# Revit family: Lodlinor
name_source: partatom
category: Generic Models
units: mm (PartAtom-declared; Revit-internal decimal feet)

## family parameters
Always vertical = Yes
Can host rebar = No
Cut with Voids When Loaded = No
Part Type = Normal
Room Calculation Point = No
Round Connector Dimension = Use Diameter
Shared = No
Work Plane-Based = No

## types (7) — shared parameters
2 = No
Height = 7000 mm  [stored 22.9659 ft]
Height_to_wheel = 6880 mm
Manufacturer = Saxi Vägg AB
URL = www.saxi.se
langd_rep = 6410 mm  [stored 21.0302 ft]

## per-type parameters (varying)
| type | 10 | 5 | 6 | 7 | 8 | 9 | Length_straight | NO_ROPES | beam_length |
| Saxi Lodlinor 4 | No | No | No | No | No | No | 2550 mm  [stored 8.36614 ft] | 4 | 4000 mm  [stored 13.1234 ft] |
| Saxi Lodlinor 5 | No | Yes | No | No | No | No | 3297 mm  [stored 10.8169 ft] | 5 | 4570 mm  [stored 14.9934 ft] |
| Saxi Lodlinor 6 | No | No | Yes | No | No | No | 3947 mm  [stored 12.9495 ft] | 6 | 5000 mm  [stored 16.4042 ft] |
| Saxi Lodlinor 7 | No | Yes | No | Yes | No | No | 4335 mm  [stored 14.2224 ft] | 7 | 5700 mm  [stored 18.7008 ft] |
| Saxi Lodlinor 8 | No | No | Yes | No | Yes | No | 5026 mm  [stored 16.4895 ft] | 8 | 6500 mm  [stored 21.3255 ft] |
| Saxi Lodlinor 9 | No | No | Yes | No | Yes | Yes | 5769 mm  [stored 18.9272 ft] | 9 | 7000 mm  [stored 22.9659 ft] |
| Saxi Lodlinor 10 | Yes | No | Yes | No | No | No | 6366 mm | 10 | 7500 mm  [stored 24.6063 ft] |

note: column(s) folded — value = type name in every type: Model

note: [stored X ft] marks values corroborated as IEEE doubles in the binary element streams (Revit-internal decimal feet)

## geometry (parser evidence)
native form markers: Sweep x57
no freeform markers — native parametric forms only
